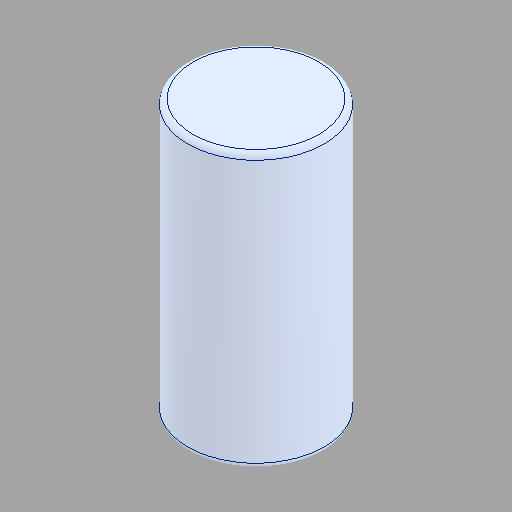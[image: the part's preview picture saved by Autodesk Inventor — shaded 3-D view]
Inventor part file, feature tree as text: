
AUTODESK INVENTOR PART (.ipt)
format: ipt  version: 2024.2 (Build 282272000, 272)  size: 98,816 bytes
history: native  units: in
note: dims shown in document units (in); Inventor stores cm internally (conversion verified against a paired STEP export)
features: fillet x1
ambient origin geometry x8: Origin, YZ Plane, XZ Plane, XY Plane, X Axis, Y Axis, Z Axis, Center Point
bodies: Solid1 (feature_tree)
feature tree (1):
  fillet  "Fillet1"  [1 undecoded]
note: 1 required parameter value undecoded (feature->parameter linkage not recoverable at this tier; creation-order binding heuristic only, values carry confidence <= 0.55)
